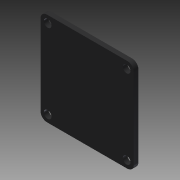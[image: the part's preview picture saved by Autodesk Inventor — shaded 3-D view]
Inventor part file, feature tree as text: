
AUTODESK INVENTOR PART (.ipt)
format: ipt  version: 2015 (Build 190159000, 159)  size: 178,688 bytes
history: native  units: mm
features: extrude x2, sketch x1
ambient origin geometry x8: Origin, YZ Plane, XZ Plane, XY Plane, X Axis, Y Axis, Z Axis, Center Point
bodies: Solid1 (feature_tree)
feature tree (3):
  sketch  "Sketch1"  dims[d0=36.0mm d1=36.0mm d8=2.2mm d9=0.0mm d13=3.0mm d14=3.0mm d15=3.0mm d16=3.0mm d17=2.5mm d18=1.8mm d19=0.0mm]
  extrude  "Extrusion2"  Depth=36.0mm
  extrude  "Extrusion3"  Depth=2.2mm TaperAngle=0.0deg
